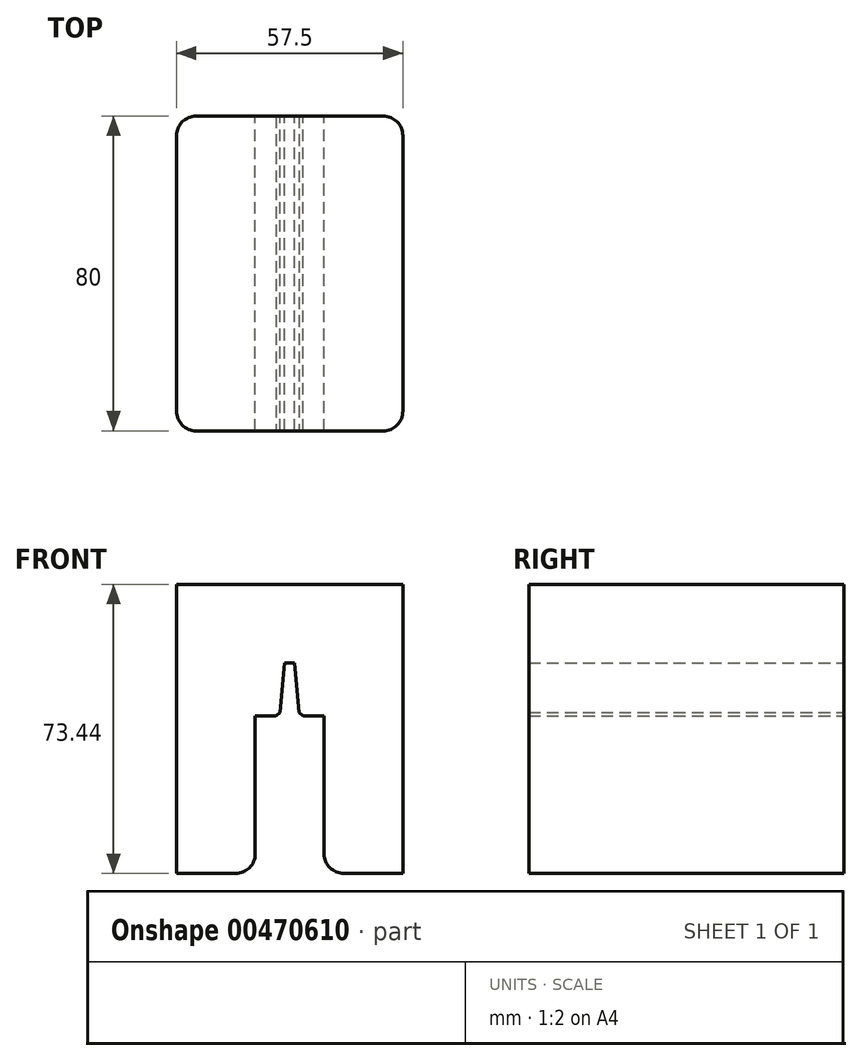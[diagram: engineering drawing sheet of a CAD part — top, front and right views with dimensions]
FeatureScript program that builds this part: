
annotation { "Feature Type Name" : "Feature", "Feature Type Description" : "" }
export const myFeature = defineFeature(function(context is Context, id is Id, definition is map)
    precondition{}
    {
        {
            var Q0;
            Q0=qCreatedBy(makeId("Front.planeOp"),FACE);
            var sketch = newSketch(context, id + "F0", { "sketchPlane" : qUnion([Q0])});
            skLineSegment(sketch, "E0", {"start": v(0, 0) * mm, "end": v(1.25, 0) * mm});
            skLineSegment(sketch, "E1", {"start": v(1.25, 0) * mm, "end": v(2.5, -13.44) * mm});
            skLineSegment(sketch, "E2", {"start": v(2.5, -13.44) * mm, "end": v(8.75, -13.44) * mm});
            skLineSegment(sketch, "E3", {"start": v(8.75, -13.44) * mm, "end": v(8.75, -53.44) * mm});
            skLineSegment(sketch, "E4", {"start": v(0, 0) * mm, "end": v(0, -44.03) * mm, "construction": true});
            skLineSegment(sketch, "E5.MirrorCS", {"start": v(0, 0) * mm, "end": v(-1.25, 0) * mm});
            skLineSegment(sketch, "E6.MirrorCS", {"start": v(-1.25, 0) * mm, "end": v(-2.5, -13.44) * mm});
            skLineSegment(sketch, "E7.MirrorCS", {"start": v(-2.5, -13.44) * mm, "end": v(-8.75, -13.44) * mm});
            skLineSegment(sketch, "E8.MirrorCS", {"start": v(-8.75, -13.44) * mm, "end": v(-8.75, -53.44) * mm});
            skLineSegment(sketch, "E9.0", {"start": v(-28.75, 6.56) * mm, "end": v(-28.75, -53.44) * mm});
            skLineSegment(sketch, "E9.3", {"start": v(0, 20) * mm, "end": v(-19.48, 20) * mm});
            skLineSegment(sketch, "E9.4", {"start": v(28.75, 6.56) * mm, "end": v(28.75, -53.44) * mm});
            skLineSegment(sketch, "E9.7", {"start": v(0, 20) * mm, "end": v(19.48, 20) * mm});
            skLineSegment(sketch, "E10", {"start": v(-19.48, 20) * mm, "end": v(-28.75, 20) * mm});
            skLineSegment(sketch, "E11", {"start": v(-28.75, 20) * mm, "end": v(-28.75, 6.56) * mm});
            skLineSegment(sketch, "E12", {"start": v(19.48, 20) * mm, "end": v(28.75, 20) * mm});
            skLineSegment(sketch, "E13", {"start": v(28.75, 20) * mm, "end": v(28.75, 6.56) * mm});
            skLineSegment(sketch, "E14", {"start": v(-28.75, -53.44) * mm, "end": v(-8.75, -53.44) * mm});
            skLineSegment(sketch, "E15", {"start": v(8.75, -53.44) * mm, "end": v(28.75, -53.44) * mm});
            skSolve(sketch);
        }
        {
            var Q0;
            Q0=makeQuery(id+"F0.imprint","IMPRINT",FACE,{"disambiguationData":[TD([[makeQuery(id+"F0.imprint","IMPRINT",EDGE,{"derivedFrom":sQuery(id+"F0.wireOp",EDGE,"E0")}),1.0]])]});
            extrude(context, id + "F1", {"entities" : qUnion([Q0]), "depth" : 80 * mm});
        }
        {
            var Q0;
            Q0=makeQuery(id+"F1.opExtrude","CAP_EDGE",EDGE,{"disambiguationData":[OSD([sQuery(id+"F0.wireOp",EDGE,"E9.4"),sQuery(id+"F0.wireOp",EDGE,"E13")])],"isStart":false});
            var Q1;
            Q1=makeQuery(id+"F1.opExtrude","CAP_EDGE",EDGE,{"disambiguationData":[OSD([sQuery(id+"F0.wireOp",EDGE,"E9.0"),sQuery(id+"F0.wireOp",EDGE,"E11")])],"isStart":false});
            var Q2;
            Q2=makeQuery(id+"F1.opExtrude","CAP_EDGE",EDGE,{"disambiguationData":[OSD([sQuery(id+"F0.wireOp",EDGE,"E9.4"),sQuery(id+"F0.wireOp",EDGE,"E13")])],"isStart":true});
            var Q3;
            Q3=makeQuery(id+"F1.opExtrude","SWEPT_EDGE",EDGE,{"disambiguationData":[OSD([sQuery(id+"F0.wireOp",EDGE,"E8.MirrorCS"),sQuery(id+"F0.wireOp",EDGE,"E14")])]});
            var Q4;
            Q4=makeQuery(id+"F1.opExtrude","SWEPT_EDGE",EDGE,{"disambiguationData":[OSD([sQuery(id+"F0.wireOp",EDGE,"E3"),sQuery(id+"F0.wireOp",EDGE,"E15")])]});
            var Q5;
            Q5=makeQuery(id+"F1.opExtrude","CAP_EDGE",EDGE,{"disambiguationData":[OSD([sQuery(id+"F0.wireOp",EDGE,"E9.0"),sQuery(id+"F0.wireOp",EDGE,"E11")])],"isStart":true});
            fillet(context, id + "F2", {"entities" : qUnion([Q0, Q1, Q2, Q3, Q4, Q5]), "radius" : 5 * mm, "tangentPropagation" : true, "allowEdgeOverflow" : false});
        }
        {
            var Q0;
            Q0=makeQuery(id+"F1.opExtrude","SWEPT_EDGE",EDGE,{"disambiguationData":[OSD([sQuery(id+"F0.wireOp",EDGE,"E1"),sQuery(id+"F0.wireOp",EDGE,"E2")])]});
            var Q1;
            Q1=makeQuery(id+"F1.opExtrude","SWEPT_EDGE",EDGE,{"disambiguationData":[OSD([sQuery(id+"F0.wireOp",EDGE,"E6.MirrorCS"),sQuery(id+"F0.wireOp",EDGE,"E7.MirrorCS")])]});
            chamfer(context, id + "F3", {"entities" : qUnion([Q0, Q1]), "width" : 1 * mm, "tangentPropagation" : true});
        }
    });
